# Revit family: Leesti Pendant Indirect 1' 2' 3' 4' 8' Revit Family 06-09-2017
name_source: partatom
category: Lighting Fixtures
revit_build: Autodesk Revit 2014 (Build: 20130308_1515(x64)
units: mm (PartAtom-declared; Revit-internal decimal feet)

## types (5) — shared parameters
Color Filter = 16777215
Dimming Lamp Color Temperature Shift = <None>
Tilt Angle = 90.00°
finish = Metal, Paint Finish, White, Matte

## per-type parameters (varying)
| type | 1st wire 1' | 1st wire 2' | 1st wire 3' | 1st wire 4' | 1st wire 8' | Emit from Line Length | Photometric Web File | Run |
| Leesti Pendant Direct 2' | No | Yes | No | No | No | 1' - 11 1/2" | Leesti Pendant Direct 2'.IES | 2' - 0" |
| Leesti Pendant Direct 4' | No | No | No | Yes | No | 3' - 10" | Leesti Pendant Direct 4'.IES | 3' - 10 1/2" |
| Leesti Pendant Direct 1' | Yes | No | No | No | No | 1' - 0 1/2" | Leesti Pendant Direct 1'.IES | 1' - 1" |
| Leesti Pendant Direct 3' | No | No | Yes | No | No | 2' - 11" | Leesti Pendant Direct 3'.IES | 2' - 11 1/2" |
| Leesti Pendant Direct 8' | No | No | No | No | Yes | 7' - 8" | Leesti Pendant Direct 4'.IES | 7' - 8 1/2" |

## geometry (parser evidence)
native form markers: Sweep x1
no freeform markers — native parametric forms only
